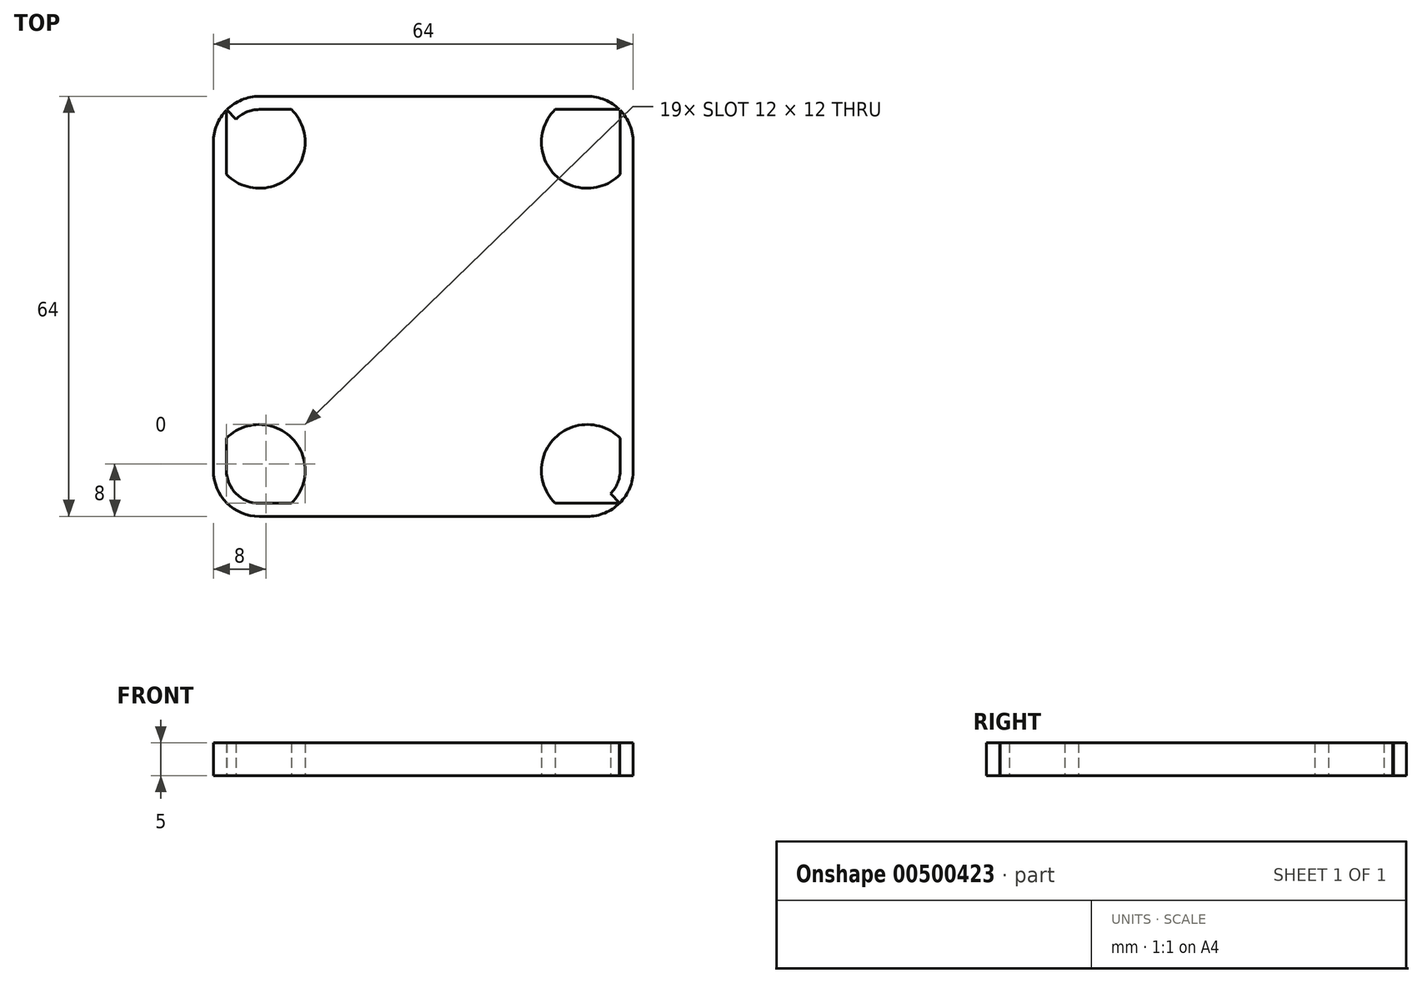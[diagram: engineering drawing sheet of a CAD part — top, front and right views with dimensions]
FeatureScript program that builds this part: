
annotation { "Feature Type Name" : "Feature", "Feature Type Description" : "" }
export const myFeature = defineFeature(function(context is Context, id is Id, definition is map)
    precondition{}
    {
        {
            var Q0;
            Q0=qCreatedBy(makeId("Top.planeOp"),FACE);
            var sketch = newSketch(context, id + "F0", { "sketchPlane" : qUnion([Q0])});
            skLineSegment(sketch, "E0.bottom", {"start": v(30, 30) * mm, "end": v(-30, 30) * mm});
            skLineSegment(sketch, "E0.top", {"start": v(30, -30) * mm, "end": v(-30, -30) * mm});
            skLineSegment(sketch, "E0.left", {"start": v(30, 30) * mm, "end": v(30, -30) * mm});
            skLineSegment(sketch, "E0.right", {"start": v(-30, 30) * mm, "end": v(-30, -30) * mm});
            skPoint(sketch, "E0.middle", {"position": v(0, 0) * mm});
            skLineSegment(sketch, "E1", {"start": v(-30, 30) * mm, "end": v(30, -30) * mm});
            skLineSegment(sketch, "E2", {"start": v(-30, -30) * mm, "end": v(30, 30) * mm});
            skCircle(sketch, "E3", {"center": v(-25, 25) * mm, "radius": 5 * mm});
            skCircle(sketch, "E4", {"center": v(25, 25) * mm, "radius": 5 * mm});
            skCircle(sketch, "E5", {"center": v(25, -25) * mm, "radius": 5 * mm});
            skCircle(sketch, "E6", {"center": v(-25, -25) * mm, "radius": 5 * mm});
            skLineSegment(sketch, "E7.bottom", {"start": v(32, 32) * mm, "end": v(-32, 32) * mm});
            skLineSegment(sketch, "E7.top", {"start": v(32, -32) * mm, "end": v(-32, -32) * mm});
            skLineSegment(sketch, "E7.left", {"start": v(32, 32) * mm, "end": v(32, -32) * mm});
            skLineSegment(sketch, "E7.right", {"start": v(-32, 32) * mm, "end": v(-32, -32) * mm});
            skCircle(sketch, "E8", {"center": v(-25, 25) * mm, "radius": 7 * mm});
            skCircle(sketch, "E9", {"center": v(25, 25) * mm, "radius": 7 * mm});
            skCircle(sketch, "E10", {"center": v(25, -25) * mm, "radius": 7 * mm});
            skCircle(sketch, "E11", {"center": v(-25, -25) * mm, "radius": 7 * mm});
            skSolve(sketch);
        }
        {
            var Q0;
            {var subQ0=sQuery(id+"F0.wireOp",EDGE,"E9");var subQ1=sQuery(id+"F0.wireOp",EDGE,"E0.bottom");var subQ2=makeQuery(id+"F0.imprint","INTERSECT",VERTEX,{"disambiguationData":[OD(1.0)],"derivedFrom":[subQ1,subQ0]});Q0=makeQuery(id+"F0.imprint","IMPRINT",FACE,{"disambiguationData":[TD([[makeQuery(id+"F0.imprint","IMPRINT",EDGE,{"disambiguationData":[TD([[subQ2,-1.0]])],"derivedFrom":subQ1}),-1.0]])]});}
            var Q1;
            {var subQ0=sQuery(id+"F0.wireOp",EDGE,"E10");var subQ1=sQuery(id+"F0.wireOp",EDGE,"E0.top");var subQ2=makeQuery(id+"F0.imprint","INTERSECT",VERTEX,{"disambiguationData":[OD(1.0)],"derivedFrom":[subQ1,subQ0]});Q1=makeQuery(id+"F0.imprint","IMPRINT",FACE,{"disambiguationData":[TD([[makeQuery(id+"F0.imprint","IMPRINT",EDGE,{"disambiguationData":[TD([[subQ2,-1.0]])],"derivedFrom":subQ1}),1.0]])]});}
            var Q2;
            {var subQ0=sQuery(id+"F0.wireOp",EDGE,"E9");var subQ1=sQuery(id+"F0.wireOp",EDGE,"E0.left");var subQ2=makeQuery(id+"F0.imprint","INTERSECT",VERTEX,{"disambiguationData":[OD(1.0)],"derivedFrom":[subQ1,subQ0]});Q2=makeQuery(id+"F0.imprint","IMPRINT",FACE,{"disambiguationData":[TD([[makeQuery(id+"F0.imprint","IMPRINT",EDGE,{"disambiguationData":[TD([[subQ2,-1.0]])],"derivedFrom":subQ1}),1.0]])]});}
            var Q3;
            {var subQ0=sQuery(id+"F0.wireOp",EDGE,"E8");var subQ1=sQuery(id+"F0.wireOp",EDGE,"E0.right");var subQ2=makeQuery(id+"F0.imprint","INTERSECT",VERTEX,{"disambiguationData":[OD(1.0)],"derivedFrom":[subQ1,subQ0]});Q3=makeQuery(id+"F0.imprint","IMPRINT",FACE,{"disambiguationData":[TD([[makeQuery(id+"F0.imprint","IMPRINT",EDGE,{"disambiguationData":[TD([[subQ2,-1.0]])],"derivedFrom":subQ1}),-1.0]])]});}
            var Q4;
            {var subQ0=sQuery(id+"F0.wireOp",EDGE,"E9");var subQ1=sQuery(id+"F0.wireOp",EDGE,"E0.bottom");var subQ2=makeQuery(id+"F0.imprint","INTERSECT",VERTEX,{"disambiguationData":[OD(0.0)],"derivedFrom":[subQ1,subQ0]});Q4=makeQuery(id+"F0.imprint","IMPRINT",FACE,{"disambiguationData":[TD([[makeQuery(id+"F0.imprint","IMPRINT",EDGE,{"disambiguationData":[TD([[subQ2,-1.0]])],"derivedFrom":subQ1}),-1.0]])]});}
            var Q5;
            {var subQ0=sQuery(id+"F0.wireOp",EDGE,"E8");var subQ1=sQuery(id+"F0.wireOp",EDGE,"E0.bottom");var subQ2=makeQuery(id+"F0.imprint","INTERSECT",VERTEX,{"disambiguationData":[OD(0.0)],"derivedFrom":[subQ1,subQ0]});Q5=makeQuery(id+"F0.imprint","IMPRINT",FACE,{"disambiguationData":[TD([[makeQuery(id+"F0.imprint","IMPRINT",EDGE,{"disambiguationData":[TD([[subQ2,-1.0]])],"derivedFrom":subQ1}),-1.0]])]});}
            var Q6;
            {var subQ0=sQuery(id+"F0.wireOp",EDGE,"E10");var subQ1=sQuery(id+"F0.wireOp",EDGE,"E0.top");var subQ2=makeQuery(id+"F0.imprint","INTERSECT",VERTEX,{"disambiguationData":[OD(0.0)],"derivedFrom":[subQ1,subQ0]});Q6=makeQuery(id+"F0.imprint","IMPRINT",FACE,{"disambiguationData":[TD([[makeQuery(id+"F0.imprint","IMPRINT",EDGE,{"disambiguationData":[TD([[subQ2,-1.0]])],"derivedFrom":subQ1}),1.0]])]});}
            var Q7;
            {var subQ0=sQuery(id+"F0.wireOp",EDGE,"E11");var subQ1=sQuery(id+"F0.wireOp",EDGE,"E0.top");var subQ2=makeQuery(id+"F0.imprint","INTERSECT",VERTEX,{"disambiguationData":[OD(0.0)],"derivedFrom":[subQ1,subQ0]});Q7=makeQuery(id+"F0.imprint","IMPRINT",FACE,{"disambiguationData":[TD([[makeQuery(id+"F0.imprint","IMPRINT",EDGE,{"disambiguationData":[TD([[subQ2,-1.0]])],"derivedFrom":subQ1}),1.0]])]});}
            var Q8;
            {var subQ0=sQuery(id+"F0.wireOp",EDGE,"E9");var subQ1=sQuery(id+"F0.wireOp",EDGE,"E0.left");var subQ2=makeQuery(id+"F0.imprint","INTERSECT",VERTEX,{"disambiguationData":[OD(0.0)],"derivedFrom":[subQ1,subQ0]});Q8=makeQuery(id+"F0.imprint","IMPRINT",FACE,{"disambiguationData":[TD([[makeQuery(id+"F0.imprint","IMPRINT",EDGE,{"disambiguationData":[TD([[subQ2,-1.0]])],"derivedFrom":subQ1}),1.0]])]});}
            var Q9;
            {var subQ0=sQuery(id+"F0.wireOp",EDGE,"E10");var subQ1=sQuery(id+"F0.wireOp",EDGE,"E0.left");var subQ2=makeQuery(id+"F0.imprint","INTERSECT",VERTEX,{"disambiguationData":[OD(0.0)],"derivedFrom":[subQ1,subQ0]});Q9=makeQuery(id+"F0.imprint","IMPRINT",FACE,{"disambiguationData":[TD([[makeQuery(id+"F0.imprint","IMPRINT",EDGE,{"disambiguationData":[TD([[subQ2,-1.0]])],"derivedFrom":subQ1}),1.0]])]});}
            var Q10;
            {var subQ0=sQuery(id+"F0.wireOp",EDGE,"E8");var subQ1=sQuery(id+"F0.wireOp",EDGE,"E0.right");var subQ2=makeQuery(id+"F0.imprint","INTERSECT",VERTEX,{"disambiguationData":[OD(0.0)],"derivedFrom":[subQ1,subQ0]});Q10=makeQuery(id+"F0.imprint","IMPRINT",FACE,{"disambiguationData":[TD([[makeQuery(id+"F0.imprint","IMPRINT",EDGE,{"disambiguationData":[TD([[subQ2,-1.0]])],"derivedFrom":subQ1}),-1.0]])]});}
            var Q11;
            {var subQ0=sQuery(id+"F0.wireOp",EDGE,"E11");var subQ1=sQuery(id+"F0.wireOp",EDGE,"E0.right");var subQ2=makeQuery(id+"F0.imprint","INTERSECT",VERTEX,{"disambiguationData":[OD(0.0)],"derivedFrom":[subQ1,subQ0]});Q11=makeQuery(id+"F0.imprint","IMPRINT",FACE,{"disambiguationData":[TD([[makeQuery(id+"F0.imprint","IMPRINT",EDGE,{"disambiguationData":[TD([[subQ2,-1.0]])],"derivedFrom":subQ1}),-1.0]])]});}
            var Q12;
            {var subQ0=sQuery(id+"F0.wireOp",EDGE,"E8");var subQ1=sQuery(id+"F0.wireOp",EDGE,"E0.right");var subQ2=makeQuery(id+"F0.imprint","INTERSECT",VERTEX,{"disambiguationData":[OD(0.0)],"derivedFrom":[subQ1,subQ0]});Q12=makeQuery(id+"F0.imprint","IMPRINT",FACE,{"disambiguationData":[TD([[makeQuery(id+"F0.imprint","IMPRINT",EDGE,{"disambiguationData":[TD([[subQ2,-1.0]])],"derivedFrom":subQ1}),1.0]])]});}
            var Q13;
            {var subQ0=sQuery(id+"F0.wireOp",EDGE,"E9");var subQ1=sQuery(id+"F0.wireOp",EDGE,"E0.bottom");var subQ2=makeQuery(id+"F0.imprint","INTERSECT",VERTEX,{"disambiguationData":[OD(0.0)],"derivedFrom":[subQ1,subQ0]});Q13=makeQuery(id+"F0.imprint","IMPRINT",FACE,{"disambiguationData":[TD([[makeQuery(id+"F0.imprint","IMPRINT",EDGE,{"disambiguationData":[TD([[subQ2,-1.0]])],"derivedFrom":subQ1}),1.0]])]});}
            var Q14;
            {var subQ0=sQuery(id+"F0.wireOp",EDGE,"E9");var subQ1=sQuery(id+"F0.wireOp",EDGE,"E0.left");var subQ2=makeQuery(id+"F0.imprint","INTERSECT",VERTEX,{"disambiguationData":[OD(0.0)],"derivedFrom":[subQ1,subQ0]});Q14=makeQuery(id+"F0.imprint","IMPRINT",FACE,{"disambiguationData":[TD([[makeQuery(id+"F0.imprint","IMPRINT",EDGE,{"disambiguationData":[TD([[subQ2,-1.0]])],"derivedFrom":subQ1}),-1.0]])]});}
            var Q15;
            {var subQ0=sQuery(id+"F0.wireOp",EDGE,"E5");var subQ1=sQuery(id+"F0.wireOp",EDGE,"E0.left");var subQ2=makeQuery(id+"F0.imprint","INTERSECT",VERTEX,{"derivedFrom":[subQ1,subQ0]});Q15=makeQuery(id+"F0.imprint","IMPRINT",FACE,{"disambiguationData":[TD([[makeQuery(id+"F0.imprint","IMPRINT",EDGE,{"disambiguationData":[TD([[subQ2,-1.0]])],"derivedFrom":subQ1}),-1.0]])]});}
            var Q16;
            {var subQ0=sQuery(id+"F0.wireOp",EDGE,"E10");var subQ1=sQuery(id+"F0.wireOp",EDGE,"E0.top");var subQ2=makeQuery(id+"F0.imprint","INTERSECT",VERTEX,{"disambiguationData":[OD(0.0)],"derivedFrom":[subQ1,subQ0]});Q16=makeQuery(id+"F0.imprint","IMPRINT",FACE,{"disambiguationData":[TD([[makeQuery(id+"F0.imprint","IMPRINT",EDGE,{"disambiguationData":[TD([[subQ2,-1.0]])],"derivedFrom":subQ1}),-1.0]])]});}
            var Q17;
            {var subQ0=sQuery(id+"F0.wireOp",EDGE,"E6");var subQ1=sQuery(id+"F0.wireOp",EDGE,"E0.top");var subQ2=makeQuery(id+"F0.imprint","INTERSECT",VERTEX,{"derivedFrom":[subQ1,subQ0]});Q17=makeQuery(id+"F0.imprint","IMPRINT",FACE,{"disambiguationData":[TD([[makeQuery(id+"F0.imprint","IMPRINT",EDGE,{"disambiguationData":[TD([[subQ2,-1.0]])],"derivedFrom":subQ1}),-1.0]])]});}
            var Q18;
            {var subQ0=sQuery(id+"F0.wireOp",EDGE,"E6");var subQ1=sQuery(id+"F0.wireOp",EDGE,"E0.right");var subQ2=makeQuery(id+"F0.imprint","INTERSECT",VERTEX,{"derivedFrom":[subQ1,subQ0]});Q18=makeQuery(id+"F0.imprint","IMPRINT",FACE,{"disambiguationData":[TD([[makeQuery(id+"F0.imprint","IMPRINT",EDGE,{"disambiguationData":[TD([[subQ2,-1.0]])],"derivedFrom":subQ1}),1.0]])]});}
            var Q19;
            {var subQ0=sQuery(id+"F0.wireOp",EDGE,"E3");var subQ1=sQuery(id+"F0.wireOp",EDGE,"E0.bottom");var subQ2=makeQuery(id+"F0.imprint","INTERSECT",VERTEX,{"derivedFrom":[subQ1,subQ0]});Q19=makeQuery(id+"F0.imprint","IMPRINT",FACE,{"disambiguationData":[TD([[makeQuery(id+"F0.imprint","IMPRINT",EDGE,{"disambiguationData":[TD([[subQ2,-1.0]])],"derivedFrom":subQ1}),1.0]])]});}
            extrude(context, id + "F1", {"entities" : qUnion([Q0, Q1, Q2, Q3, Q4, Q5, Q6, Q7, Q8, Q9, Q10, Q11, Q12, Q13, Q14, Q15, Q16, Q17, Q18, Q19]), "depth" : 5 * mm});
        }
    });
